# Revit family: DAL_A3-DTI-SL6
name_source: partatom
category: Doors
revit_build: Autodesk Revit 2016 (Build: 20150220_1215(x64)
units: mm (PartAtom-declared; Revit-internal decimal feet)

## family parameters
Always vertical = Yes
Cut with Voids When Loaded = No
Host = Wall
Room Calculation Point = No
Shared = No

## types (1)
- SL6
    Assembly Code = B2030230
    Frame Material = Meranti Wood
    Frame Thickness = 60 mm  [stored 0.19685 ft]
    Frame Width = 48 mm  [stored 0.15748 ft]
    Function = Interior
    Glass Material = Glass
    Height = 2080 mm  [stored 6.82415 ft]
    Manufacturer = AC Doors
    Manufacturer Code = SL6
    Middle = 526 mm  [stored 1.72572 ft]
    Model = AC Combination Sidelights
    Offset = 100 mm  [stored 0.328084 ft]
    Panel Height = 2032 mm
    Panel Material = Meranti Wood
    Panel Thickness = 44 mm  [stored 0.144357 ft]
    URL = www.acdoors.co.za
    Wall Closure = By host
    Width = 2200 mm

note: [stored X ft] marks values corroborated as IEEE doubles in the binary element streams (Revit-internal decimal feet)

## geometry (parser evidence)
native form markers: Sweep x7
no freeform markers — native parametric forms only
